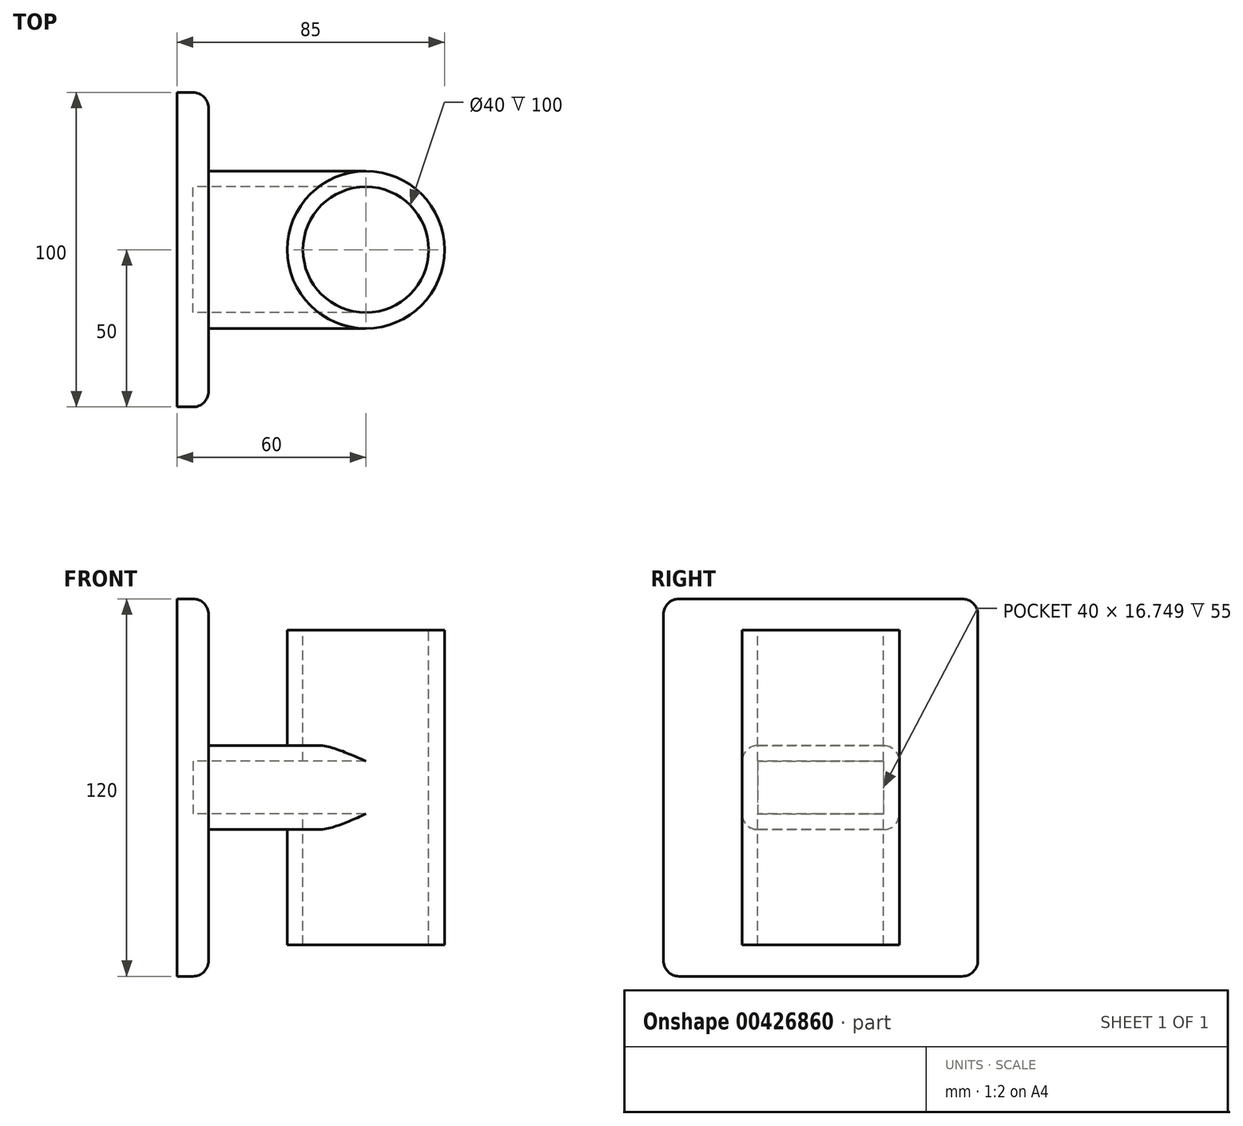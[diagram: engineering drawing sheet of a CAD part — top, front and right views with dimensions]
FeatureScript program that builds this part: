
annotation { "Feature Type Name" : "Feature", "Feature Type Description" : "" }
export const myFeature = defineFeature(function(context is Context, id is Id, definition is map)
    precondition{}
    {
        {
            var Q0;
            Q0=qCreatedBy(makeId("Front.planeOp"),FACE);
            var sketch = newSketch(context, id + "F0", { "sketchPlane" : qUnion([Q0])});
            skLineSegment(sketch, "E0.bottom", {"start": v(-25, 13.37) * mm, "end": v(25, 13.37) * mm});
            skLineSegment(sketch, "E0.top", {"start": v(-25, -13.37) * mm, "end": v(25, -13.37) * mm});
            skLineSegment(sketch, "E0.left", {"start": v(-25, 13.37) * mm, "end": v(-25, -13.37) * mm});
            skLineSegment(sketch, "E0.right", {"start": v(25, 13.37) * mm, "end": v(25, -13.37) * mm});
            skPoint(sketch, "E0.middle", {"position": v(0, 0) * mm});
            skLineSegment(sketch, "E1.bottom", {"start": v(-35, 60) * mm, "end": v(-25, 60) * mm});
            skLineSegment(sketch, "E1.top", {"start": v(-35, -60) * mm, "end": v(-25, -60) * mm});
            skLineSegment(sketch, "E1.left", {"start": v(-35, 60) * mm, "end": v(-35, -60) * mm});
            skLineSegment(sketch, "E1.right", {"start": v(-25, 60) * mm, "end": v(-25, -60) * mm});
            skPoint(sketch, "E1.middle", {"position": v(-30, 0) * mm});
            skLineSegment(sketch, "E2.bottom", {"start": v(50, 50) * mm, "end": v(25, 50) * mm});
            skLineSegment(sketch, "E2.top", {"start": v(50, -50) * mm, "end": v(25, -50) * mm});
            skLineSegment(sketch, "E2.left", {"start": v(50, 50) * mm, "end": v(50, -50) * mm});
            skLineSegment(sketch, "E2.right", {"start": v(25, 50) * mm, "end": v(25, -50) * mm});
            skPoint(sketch, "E2.middle", {"position": v(37.5, 0) * mm});
            skSolve(sketch);
        }
        {
            var Q0;
            {var subQ2=sQuery(id+"F0.wireOp",EDGE,"E1.bottom");Q0=makeQuery(id+"F0.imprint","IMPRINT",FACE,{"disambiguationData":[TD([[makeQuery(id+"F0.imprint","IMPRINT",EDGE,{"derivedFrom":subQ2}),-1.0]])]});}
            extrude(context, id + "F1", {"entities" : qUnion([Q0]), "endBound" : BoundingType.SYMMETRIC, "depth" : 100 * mm});
        }
        {
            var Q0;
            {var subQ0=sQuery(id+"F0.wireOp",EDGE,"E0.bottom");Q0=makeQuery(id+"F0.imprint","IMPRINT",FACE,{"disambiguationData":[TD([[makeQuery(id+"F0.imprint","IMPRINT",EDGE,{"derivedFrom":subQ0}),-1.0]])]});}
            extrude(context, id + "F2", {"entities" : qUnion([Q0]), "operationType" : NewBodyOperationType.ADD, "endBound" : BoundingType.SYMMETRIC, "depth" : 50 * mm});
        }
        {
            var Q0;
            {var subQ2=sQuery(id+"F0.wireOp",EDGE,"E2.bottom");Q0=makeQuery(id+"F0.imprint","IMPRINT",FACE,{"disambiguationData":[TD([[makeQuery(id+"F0.imprint","IMPRINT",EDGE,{"derivedFrom":subQ2}),1.0]])]});}
            var Q1;
            Q1=sQuery(id+"F0.wireOp",EDGE,"E2.right");
            revolve(context, id + "F3", {"operationType" : NewBodyOperationType.ADD, "entities" : qUnion([Q0]), "axis" : qUnion([Q1]), "revolveType" : RevolveType.FULL});
        }
        {
            var Q0;
            Q0=makeQuery(id+"F2.opExtrude","CAP_EDGE",EDGE,{"disambiguationData":[OSD([sQuery(id+"F0.wireOp",EDGE,"E0.bottom")])],"isStart":false});
            var Q1;
            Q1=makeQuery(id+"F2.opExtrude","CAP_EDGE",EDGE,{"disambiguationData":[OSD([sQuery(id+"F0.wireOp",EDGE,"E0.top")])],"isStart":false});
            var Q2;
            Q2=makeQuery(id+"F2.opExtrude","CAP_EDGE",EDGE,{"disambiguationData":[OSD([sQuery(id+"F0.wireOp",EDGE,"E0.bottom")])],"isStart":true});
            var Q3;
            Q3=makeQuery(id+"F2.opExtrude","CAP_EDGE",EDGE,{"disambiguationData":[OSD([sQuery(id+"F0.wireOp",EDGE,"E0.top")])],"isStart":true});
            var Q4;
            Q4=makeQuery(id+"F1.opExtrude","CAP_EDGE",EDGE,{"disambiguationData":[OSD([sQuery(id+"F0.wireOp",EDGE,"E1.right")])],"isStart":true});
            var Q5;
            Q5=makeQuery(id+"F1.opExtrude","SWEPT_EDGE",EDGE,{"disambiguationData":[OSD([sQuery(id+"F0.wireOp",EDGE,"E1.bottom"),sQuery(id+"F0.wireOp",EDGE,"E1.right")])]});
            var Q6;
            Q6=makeQuery(id+"F1.opExtrude","CAP_EDGE",EDGE,{"disambiguationData":[OSD([sQuery(id+"F0.wireOp",EDGE,"E1.bottom")])],"isStart":true});
            var Q7;
            Q7=makeQuery(id+"F1.opExtrude","SWEPT_EDGE",EDGE,{"disambiguationData":[OSD([sQuery(id+"F0.wireOp",EDGE,"E1.top"),sQuery(id+"F0.wireOp",EDGE,"E1.right")])]});
            var Q8;
            Q8=makeQuery(id+"F1.opExtrude","CAP_EDGE",EDGE,{"disambiguationData":[OSD([sQuery(id+"F0.wireOp",EDGE,"E1.top")])],"isStart":true});
            var Q9;
            Q9=makeQuery(id+"F1.opExtrude","CAP_EDGE",EDGE,{"disambiguationData":[OSD([sQuery(id+"F0.wireOp",EDGE,"E1.right")])],"isStart":false});
            var Q10;
            Q10=makeQuery(id+"F1.opExtrude","CAP_EDGE",EDGE,{"disambiguationData":[OSD([sQuery(id+"F0.wireOp",EDGE,"E1.bottom")])],"isStart":false});
            var Q11;
            Q11=makeQuery(id+"F1.opExtrude","CAP_EDGE",EDGE,{"disambiguationData":[OSD([sQuery(id+"F0.wireOp",EDGE,"E1.top")])],"isStart":false});
            fillet(context, id + "F4", {"entities" : qUnion([Q0, Q1, Q2, Q3, Q4, Q5, Q6, Q7, Q8, Q9, Q10, Q11]), "radius" : 5 * mm, "tangentPropagation" : true, "allowEdgeOverflow" : false});
        }
        {
            var Q0;
            Q0=makeQuery(id+"F3.opRevolve","SWEPT_FACE",FACE,{"disambiguationData":[OSD([sQuery(id+"F0.wireOp",EDGE,"E2.bottom")])]});
            var Q1;
            Q1=makeQuery(id+"F3.opRevolve","SWEPT_FACE",FACE,{"disambiguationData":[OSD([sQuery(id+"F0.wireOp",EDGE,"E2.top")])]});
            shell(context, id + "F5", {"entities" : qUnion([Q0, Q1]), "thickness" : 5 * mm});
        }
    });
